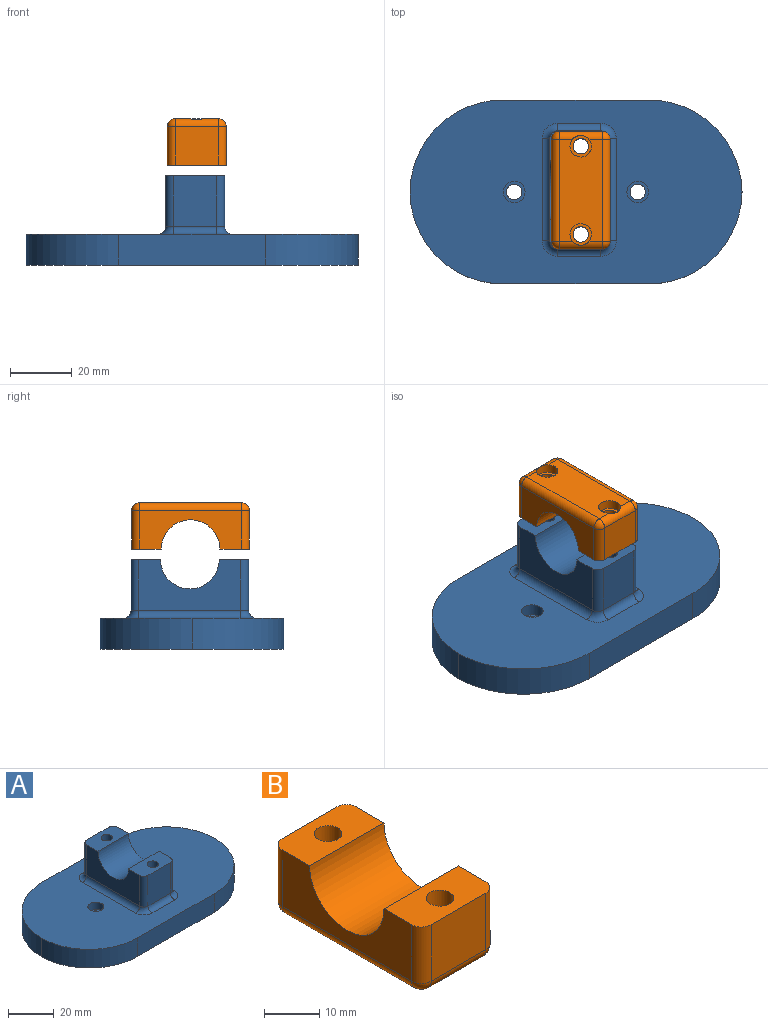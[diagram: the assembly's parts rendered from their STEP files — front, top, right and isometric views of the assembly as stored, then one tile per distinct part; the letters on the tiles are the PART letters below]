
ASSEMBLY  parts=2 mates=1
PART A: 59 faces, bbox 107.5x59.5x29 mm
  f0: plane 107.5x59.5mm, normal (0,0,-1), area 5541.1mm2, adj f3,f4,f8,f9,f10,f11,f12,f13
  f1: cylinder r=2.5mm len=23mm, axis (0,0,1), area 361.3mm2, adj f17,f25,f28,f31,f43,f45,f46
  f2: cylinder r=2.5mm len=23mm, axis (0,0,1), area 361.3mm2, adj f6,f34,f37,f40,f41,f42,f44
  f3: cylinder r=2.5mm len=6mm, axis (0,0,-1), area 94.2mm2, adj f0,f22
  f4: cylinder r=2.5mm len=6mm, axis (0,0,-1), area 94.2mm2, adj f0,f20
  f5: plane 33.1x16.5mm, normal (-1,0,0), area 404.4mm2, adj f6,f17,f18,f49,f55,f58
  f6: plane 19x9.55mm, normal (0,0,1), area 159.1mm2, adj f2,f5,f14,f16,f18,f52,f58
  f7: plane 107.5x59.5mm, normal (0,0,1), area 4533.8mm2, adj f8,f9,f10,f11,f12,f13,f19,f21
  f8: plane 47.5x10mm, normal (0,-1,0), area 475mm2, adj f0,f7,f9,f13
  f9: cylinder r=30mm len=30mm, axis (0,0,-1), area 468.7mm2, adj f0,f7,f8,f10
  f10: cylinder r=30mm len=30mm, axis (0,0,-1), area 468.7mm2, adj f0,f7,f9,f11
  f11: plane 47.5x10mm, normal (0,1,0), area 475mm2, adj f0,f7,f10,f12
  f12: cylinder r=30mm len=30mm, axis (0,0,-1), area 468.7mm2, adj f0,f7,f11,f13
  f13: cylinder r=30mm len=30mm, axis (0,0,-1), area 468.7mm2, adj f0,f7,f8,f12
  f14: plane 16.5x14mm, normal (0,1,0), area 231mm2, adj f6,f52,f56,f58
  f15: plane 16.5x14mm, normal (0,-1,0), area 231mm2, adj f17,f47,f49,f50
  f16: plane 33.1x16.5mm, normal (1,0,0), area 404.4mm2, adj f6,f17,f18,f47,f51,f52
  f17: plane 19x9.55mm, normal (0,0,1), area 159.1mm2, adj f1,f5,f15,f16,f18,f47,f49
  f18: cylinder r=9.5mm len=19mm, axis (-1,0,0), area 567.1mm2, adj f5,f6,f16,f17
  f19: cylinder r=3.5mm len=7mm, axis (0,0,1), area 88mm2, adj f7,f20
  f20: plane 7x7mm, normal (0,0,1), area 18.8mm2, adj f4,f19
  f21: cylinder r=3.5mm len=7mm, axis (0,0,1), area 88mm2, adj f7,f22
  f22: plane 7x7mm, normal (0,0,1), area 18.8mm2, adj f3,f21
  f23: plane 6x2.5mm, normal (0.5,-0.87,0), area 17.3mm2, adj f0,f24,f25,f27,f45
  f24: plane 6x2.5mm, normal (-0.5,-0.87,0), area 17.3mm2, adj f0,f23,f25,f29,f46
  f25: plane 2.5x0.72mm, normal (0,0,-1), area 0.3mm2, adj f1,f23,f24
  f26: plane 6x2.5mm, normal (0.5,0.87,0), area 17.3mm2, adj f0,f27,f28,f30,f43
  f27: plane 6x2.89mm, normal (1,0,0), area 17.3mm2, adj f0,f23,f26,f28,f45
  f28: plane 2.17x1.25mm, normal (0,0,-1), area 0.3mm2, adj f1,f26,f27
  f29: plane 6x2.89mm, normal (-1,0,0), area 17.3mm2, adj f0,f24,f30,f31,f46
  f30: plane 6x2.5mm, normal (-0.5,0.87,0), area 17.3mm2, adj f0,f26,f29,f31,f43
  f31: plane 2.17x1.25mm, normal (0,0,-1), area 0.3mm2, adj f1,f29,f30
  f32: plane 6x2.38mm, normal (-0.83,-0.56,0), area 17.3mm2, adj f0,f33,f34,f36,f42
  f33: plane 6x2.6mm, normal (-0.9,0.43,0), area 17.3mm2, adj f0,f32,f34,f38,f44
  f34: plane 2.49x0.82mm, normal (0,0,-1), area 0.3mm2, adj f2,f32,f33
  f35: plane 6x2.6mm, normal (0.9,-0.43,0), area 17.3mm2, adj f0,f36,f37,f39,f41
  f36: plane 6x2.88mm, normal (0.08,-1,0), area 17.3mm2, adj f0,f32,f35,f37,f42
  f37: plane 2.06x1.41mm, normal (0,0,-1), area 0.3mm2, adj f2,f35,f36
  f38: plane 6x2.88mm, normal (-0.08,1,0), area 17.3mm2, adj f0,f33,f39,f40,f44
  f39: plane 6x2.38mm, normal (0.83,0.56,0), area 17.3mm2, adj f0,f35,f38,f40,f41
  f40: plane 2.25x1.19mm, normal (0,0,-1), area 0.3mm2, adj f2,f38,f39
  f41: plane 2.49x0.82mm, normal (0,0,-1), area 0.3mm2, adj f2,f35,f39
  f42: plane 2.25x1.19mm, normal (0,0,-1), area 0.3mm2, adj f2,f32,f36
  f43: plane 2.5x0.72mm, normal (0,0,-1), area 0.3mm2, adj f1,f26,f30
  f44: plane 2.06x1.41mm, normal (0,0,-1), area 0.3mm2, adj f2,f33,f38
  f45: plane 2.17x1.25mm, normal (0,0,-1), area 0.3mm2, adj f1,f23,f27
  f46: plane 2.17x1.25mm, normal (0,0,-1), area 0.3mm2, adj f1,f24,f29
  f47: cylinder r=2.5mm len=16.5mm, axis (0,0,1), area 64.8mm2, adj f15,f16,f17,f48
  f48: torus R=5mm, axis (0,0,1), area 21mm2, adj f7,f47,f50,f51
  f49: cylinder r=2.5mm len=16.5mm, axis (0,0,-1), area 64.8mm2, adj f5,f15,f17,f53
  f50: cylinder r=2.5mm len=14mm, axis (1,0,0), area 55mm2, adj f7,f15,f48,f53
  f51: cylinder r=2.5mm len=33.1mm, axis (0,1,0), area 130mm2, adj f7,f16,f48,f54
  f52: cylinder r=2.5mm len=16.5mm, axis (0,0,-1), area 64.8mm2, adj f6,f14,f16,f54
  f53: torus R=5mm, axis (0,0,1), area 21mm2, adj f7,f49,f50,f55
  f54: torus R=5mm, axis (0,0,1), area 21mm2, adj f7,f51,f52,f56
  f55: cylinder r=2.5mm len=33.1mm, axis (0,-1,0), area 130mm2, adj f5,f7,f53,f57
  f56: cylinder r=2.5mm len=14mm, axis (-1,0,0), area 55mm2, adj f7,f14,f54,f57
  f57: torus R=5mm, axis (0,0,1), area 21mm2, adj f7,f55,f56,f58
  f58: cylinder r=2.5mm len=16.5mm, axis (0,0,1), area 64.8mm2, adj f5,f6,f14,f57
PART B: 26 faces, bbox 19x38.1x15 mm
  f0: cylinder r=2.5mm len=12mm, axis (0,0,1), area 188.5mm2, adj f2,f13
  f1: cylinder r=2.5mm len=12mm, axis (0,0,1), area 188.5mm2, adj f7,f11
  f2: plane 19x9.55mm, normal (0,0,1), area 159.1mm2, adj f0,f3,f5,f6,f9,f14,f19
  f3: plane 33.1x12.5mm, normal (-1,0,0), area 272mm2, adj f2,f7,f9,f19,f23,f25
  f4: plane 14x12.5mm, normal (0,-1,0), area 175mm2, adj f7,f16,f22,f25
  f5: plane 33.1x12.5mm, normal (1,0,0), area 272mm2, adj f2,f7,f9,f14,f16,f17
  f6: plane 14x12.5mm, normal (0,1,0), area 175mm2, adj f2,f14,f18,f19
  f7: plane 19x9.55mm, normal (0,0,1), area 159.1mm2, adj f1,f3,f4,f5,f9,f16,f25
  f8: plane 33.1x14mm, normal (0,0,-1), area 395.5mm2, adj f10,f12,f17,f18,f22,f23
  f9: cylinder r=9.5mm len=19mm, axis (-1,0,0), area 567.1mm2, adj f2,f3,f5,f7
  f10: cylinder r=3.5mm len=7mm, axis (0,0,-1), area 65mm2, adj f8,f11,f22
  f11: plane 7x7mm, normal (0,0,-1), area 18.8mm2, adj f1,f10
  f12: cylinder r=3.5mm len=7mm, axis (0,0,-1), area 65mm2, adj f8,f13,f18
  f13: plane 7x7mm, normal (0,0,-1), area 18.8mm2, adj f0,f12
  f14: cylinder r=2.5mm len=12.5mm, axis (0,0,1), area 49.1mm2, adj f2,f5,f6,f15
  f15: sphere r=2.5mm, area 9.8mm2, adj f14,f17,f18
  f16: cylinder r=2.5mm len=12.5mm, axis (0,0,-1), area 49.1mm2, adj f4,f5,f7,f20
  f17: cylinder r=2.5mm len=33.1mm, axis (0,1,0), area 130mm2, adj f5,f8,f15,f20
  f18: cylinder r=2.5mm len=14mm, axis (-1,0,0), area 50.3mm2, adj f6,f8,f12,f15,f21
  f19: cylinder r=2.5mm len=12.5mm, axis (0,0,-1), area 49.1mm2, adj f2,f3,f6,f21
  f20: sphere r=2.5mm, area 9.8mm2, adj f16,f17,f22
  f21: sphere r=2.5mm, area 9.8mm2, adj f18,f19,f23
  f22: cylinder r=2.5mm len=14mm, axis (1,0,0), area 50.3mm2, adj f4,f8,f10,f20,f24
  f23: cylinder r=2.5mm len=33.1mm, axis (0,-1,0), area 130mm2, adj f3,f8,f21,f24
  f24: sphere r=2.5mm, area 9.8mm2, adj f22,f23,f25
  f25: cylinder r=2.5mm len=12.5mm, axis (0,0,1), area 49.1mm2, adj f3,f4,f7,f24
PLACE A t=(-40.02,2.97,-3.74)mm
PLACE B rot(axis=(1,0,0),180deg) t=(5.77,52.24,43.65)mm
MATE cylindrical B.f0 <-> A.f1  axis (0,0,-1) through (15.27,18.92,28.65)mm
